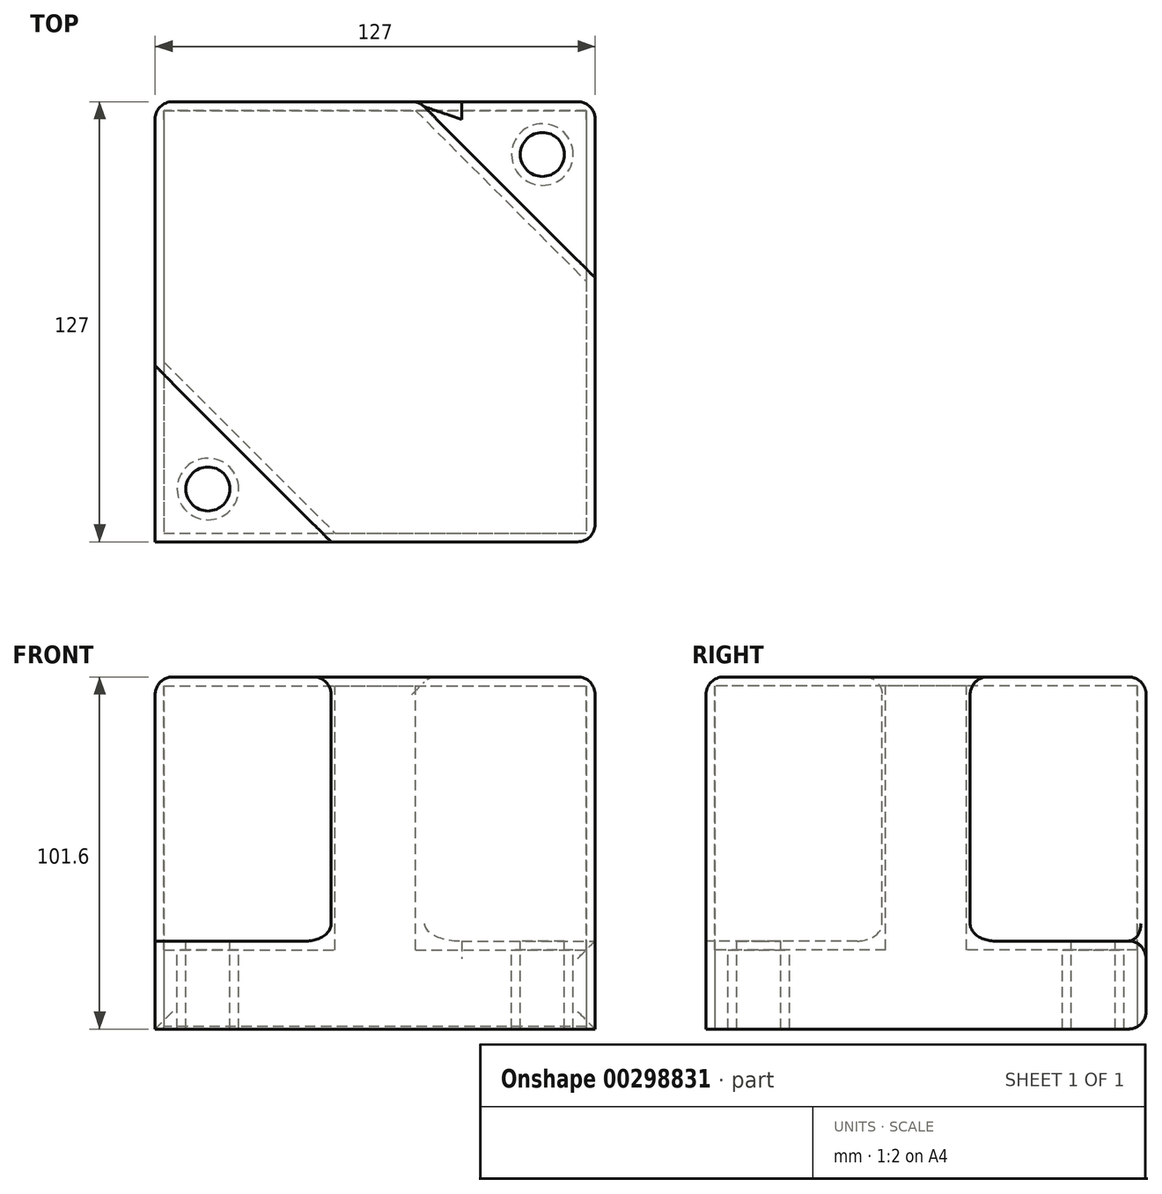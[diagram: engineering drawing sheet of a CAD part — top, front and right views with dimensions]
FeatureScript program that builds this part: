
annotation { "Feature Type Name" : "Feature", "Feature Type Description" : "" }
export const myFeature = defineFeature(function(context is Context, id is Id, definition is map)
    precondition{}
    {
        {
            var Q0;
            Q0=qCreatedBy(makeId("Top.planeOp"),FACE);
            var sketch = newSketch(context, id + "F0", { "sketchPlane" : qUnion([Q0])});
            skLineSegment(sketch, "E0.bottom", {"start": v(-64.1, 63.75) * mm, "end": v(62.9, 63.75) * mm});
            skLineSegment(sketch, "E0.top", {"start": v(-64.1, -63.25) * mm, "end": v(62.9, -63.25) * mm});
            skLineSegment(sketch, "E0.left", {"start": v(-64.1, 63.75) * mm, "end": v(-64.1, -63.25) * mm});
            skLineSegment(sketch, "E0.right", {"start": v(62.9, 63.75) * mm, "end": v(62.9, -63.25) * mm});
            skSolve(sketch);
        }
        {
            var Q0;
            Q0 = qSketchRegion(id + "F0", true);
            extrude(context, id + "F1", {"entities" : qUnion([Q0]), "depth" : 101.6 * mm});
        }
        {
            var Q0;
            Q0=makeQuery(id+"F1.opExtrude","CAP_FACE",FACE,{"disambiguationData":[OSD([sQuery(id+"F0.wireOp",EDGE,"E0.bottom"),sQuery(id+"F0.wireOp",EDGE,"E0.top"),sQuery(id+"F0.wireOp",EDGE,"E0.left"),sQuery(id+"F0.wireOp",EDGE,"E0.right")])],"isStart":false});
            var sketch = newSketch(context, id + "F2", { "sketchPlane" : qUnion([Q0])});
            skLineSegment(sketch, "E1", {"start": v(-64.1, -63.25) * mm, "end": v(-13.3, -63.25) * mm});
            skLineSegment(sketch, "E2", {"start": v(-64.1, -63.25) * mm, "end": v(-64.1, -12.45) * mm});
            skLineSegment(sketch, "E3", {"start": v(-64.1, -12.45) * mm, "end": v(-13.3, -63.25) * mm});
            skLineSegment(sketch, "E4", {"start": v(62.9, 63.75) * mm, "end": v(62.9, 12.95) * mm});
            skLineSegment(sketch, "E5", {"start": v(62.9, 63.75) * mm, "end": v(12.1, 63.75) * mm});
            skLineSegment(sketch, "E6", {"start": v(12.1, 63.75) * mm, "end": v(62.9, 12.95) * mm});
            skSolve(sketch);
        }
        {
            var Q0;
            Q0 = qSketchRegion(id + "F2", true);
            extrude(context, id + "F3", {"entities" : qUnion([Q0]), "operationType" : NewBodyOperationType.REMOVE, "oppositeDirection" : true, "depth" : 76.2 * mm});
        }
        {
            var Q0;
            Q0=makeQuery(id+"F3.boolean.opBoolean","COPY",FACE,{"derivedFrom":makeQuery(id+"F3.opExtrude","CAP_FACE",FACE,{"disambiguationData":[OSD([sQuery(id+"F2.wireOp",EDGE,"E4"),sQuery(id+"F2.wireOp",EDGE,"E5"),sQuery(id+"F2.wireOp",EDGE,"E6")])],"isStart":false})});
            var sketch = newSketch(context, id + "F4", { "sketchPlane" : qUnion([Q0])});
            skCircle(sketch, "E7", {"center": v(47.65, 48.51) * mm, "radius": 6.35 * mm});
            skCircle(sketch, "E8", {"center": v(-48.87, -48) * mm, "radius": 6.35 * mm});
            skSolve(sketch);
        }
        {
            var Q0;
            Q0=makeQuery(id+"F4.imprint","IMPRINT",FACE,{"disambiguationData":[TD([[makeQuery(id+"F4.imprint","IMPRINT",EDGE,{"derivedFrom":sQuery(id+"F4.wireOp",EDGE,"E8")}),1.0]])]});
            var Q1;
            Q1=makeQuery(id+"F4.imprint","IMPRINT",FACE,{"disambiguationData":[TD([[makeQuery(id+"F4.imprint","IMPRINT",EDGE,{"derivedFrom":sQuery(id+"F4.wireOp",EDGE,"E7")}),1.0]])]});
            extrude(context, id + "F5", {"entities" : qUnion([Q0, Q1]), "operationType" : NewBodyOperationType.REMOVE, "oppositeDirection" : true, "depth" : 203.2 * mm});
        }
        {
            var Q0;
            Q0=makeQuery(id+"F1.opExtrude","CAP_FACE",FACE,{"disambiguationData":[OSD([sQuery(id+"F0.wireOp",EDGE,"E0.bottom"),sQuery(id+"F0.wireOp",EDGE,"E0.top"),sQuery(id+"F0.wireOp",EDGE,"E0.left"),sQuery(id+"F0.wireOp",EDGE,"E0.right")])],"isStart":true});
            shell(context, id + "F6", {"entities" : qUnion([Q0]), "thickness" : 2.54 * mm});
        }
        {
            var Q0;
            Q0=makeQuery(id+"F1.opExtrude","CAP_EDGE",EDGE,{"disambiguationData":[OSD([sQuery(id+"F0.wireOp",EDGE,"E0.right")])],"isStart":false});
            var Q1;
            Q1=makeQuery(id+"F3.boolean.opBoolean","COPY",EDGE,{"derivedFrom":makeQuery(id+"F3.opExtrude","CAP_EDGE",EDGE,{"disambiguationData":[OSD([sQuery(id+"F2.wireOp",EDGE,"E6")])],"isStart":true})});
            var Q2;
            Q2=makeQuery(id+"F1.opExtrude","CAP_EDGE",EDGE,{"disambiguationData":[OSD([sQuery(id+"F0.wireOp",EDGE,"E0.bottom")])],"isStart":false});
            var Q3;
            Q3=makeQuery(id+"F3.boolean.opBoolean","COPY",EDGE,{"derivedFrom":makeQuery(id+"F3.opExtrude","SWEPT_EDGE",EDGE,{"disambiguationData":[OSD([sQuery(id+"F0.wireOp",EDGE,"E0.right"),sQuery(id+"F2.wireOp",EDGE,"E4"),sQuery(id+"F2.wireOp",EDGE,"E6")])]})});
            var Q4;
            Q4=makeQuery(id+"F3.boolean.opBoolean","COPY",EDGE,{"derivedFrom":makeQuery(id+"F3.opExtrude","SWEPT_EDGE",EDGE,{"disambiguationData":[OSD([sQuery(id+"F0.wireOp",EDGE,"E0.bottom"),sQuery(id+"F2.wireOp",EDGE,"E5"),sQuery(id+"F2.wireOp",EDGE,"E6")])]})});
            var Q5;
            Q5=makeQuery(id+"F3.boolean.opBoolean","COPY",EDGE,{"derivedFrom":makeQuery(id+"F3.opExtrude","CAP_EDGE",EDGE,{"disambiguationData":[OSD([sQuery(id+"F2.wireOp",EDGE,"E5")])],"isStart":false})});
            var Q6;
            Q6=makeQuery(id+"F3.boolean.opBoolean","COPY",EDGE,{"derivedFrom":makeQuery(id+"F3.opExtrude","CAP_EDGE",EDGE,{"disambiguationData":[OSD([sQuery(id+"F2.wireOp",EDGE,"E6")])],"isStart":false})});
            var Q7;
            Q7=makeQuery(id+"F1.opExtrude","SWEPT_EDGE",EDGE,{"disambiguationData":[OSD([sQuery(id+"F0.wireOp",EDGE,"E0.bottom"),sQuery(id+"F0.wireOp",EDGE,"E0.left")])]});
            var Q8;
            Q8=makeQuery(id+"F1.opExtrude","SWEPT_FACE",FACE,{"disambiguationData":[OSD([sQuery(id+"F0.wireOp",EDGE,"E0.bottom")])]});
            var Q9;
            Q9=makeQuery(id+"F1.opExtrude","SWEPT_EDGE",EDGE,{"disambiguationData":[OSD([sQuery(id+"F0.wireOp",EDGE,"E0.top"),sQuery(id+"F0.wireOp",EDGE,"E0.right")])]});
            var Q10;
            Q10=makeQuery(id+"F1.opExtrude","CAP_EDGE",EDGE,{"disambiguationData":[OSD([sQuery(id+"F0.wireOp",EDGE,"E0.top")])],"isStart":false});
            var Q11;
            Q11=makeQuery(id+"F3.boolean.opBoolean","COPY",EDGE,{"derivedFrom":makeQuery(id+"F3.opExtrude","CAP_EDGE",EDGE,{"disambiguationData":[OSD([sQuery(id+"F2.wireOp",EDGE,"E3")])],"isStart":true})});
            var Q12;
            Q12=makeQuery(id+"F1.opExtrude","CAP_EDGE",EDGE,{"disambiguationData":[OSD([sQuery(id+"F0.wireOp",EDGE,"E0.left")])],"isStart":false});
            var Q13;
            Q13=makeQuery(id+"F3.boolean.opBoolean","COPY",EDGE,{"derivedFrom":makeQuery(id+"F3.opExtrude","CAP_EDGE",EDGE,{"disambiguationData":[OSD([sQuery(id+"F2.wireOp",EDGE,"E4")])],"isStart":false})});
            var Q14;
            Q14=makeQuery(id+"F3.boolean.opBoolean","COPY",EDGE,{"derivedFrom":makeQuery(id+"F3.opExtrude","SWEPT_EDGE",EDGE,{"disambiguationData":[OSD([sQuery(id+"F0.wireOp",EDGE,"E0.top"),sQuery(id+"F2.wireOp",EDGE,"E1"),sQuery(id+"F2.wireOp",EDGE,"E3")])]})});
            var Q15;
            Q15=makeQuery(id+"F3.boolean.opBoolean","COPY",EDGE,{"derivedFrom":makeQuery(id+"F3.opExtrude","SWEPT_EDGE",EDGE,{"disambiguationData":[OSD([sQuery(id+"F0.wireOp",EDGE,"E0.left"),sQuery(id+"F2.wireOp",EDGE,"E2"),sQuery(id+"F2.wireOp",EDGE,"E3")])]})});
            var Q16;
            Q16=makeQuery(id+"F3.boolean.opBoolean","COPY",EDGE,{"derivedFrom":makeQuery(id+"F3.opExtrude","CAP_EDGE",EDGE,{"disambiguationData":[OSD([sQuery(id+"F2.wireOp",EDGE,"E3")])],"isStart":false})});
            var Q17;
            Q17=makeQuery(id+"F3.boolean.opBoolean","COPY",EDGE,{"derivedFrom":makeQuery(id+"F3.opExtrude","CAP_EDGE",EDGE,{"disambiguationData":[OSD([sQuery(id+"F2.wireOp",EDGE,"E1")])],"isStart":false})});
            var Q18;
            Q18=makeQuery(id+"F3.boolean.opBoolean","COPY",EDGE,{"derivedFrom":makeQuery(id+"F3.opExtrude","CAP_EDGE",EDGE,{"disambiguationData":[OSD([sQuery(id+"F2.wireOp",EDGE,"E2")])],"isStart":false})});
            var Q19;
            Q19=makeQuery(id+"F1.opExtrude","CAP_EDGE",EDGE,{"disambiguationData":[OSD([sQuery(id+"F0.wireOp",EDGE,"E0.bottom")])],"isStart":true});
            fillet(context, id + "F7", {"entities" : qUnion([Q0, Q1, Q2, Q3, Q4, Q5, Q6, Q7, Q8, Q9, Q10, Q11, Q12, Q13, Q14, Q15, Q16, Q17, Q18, Q19]), "radius" : 5.08 * mm, "tangentPropagation" : true, "allowEdgeOverflow" : false});
        }
    });
